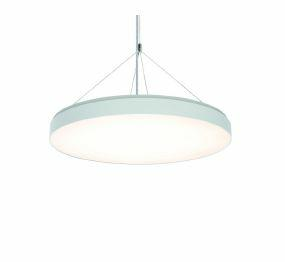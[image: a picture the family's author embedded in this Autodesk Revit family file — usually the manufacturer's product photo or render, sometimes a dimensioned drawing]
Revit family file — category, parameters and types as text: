
# Revit family: spectral_stora_stora-rp-led_4300_840_mps_c88b
name_source: partatom
category: Lighting Fixtures
revit_build: Autodesk Revit 2016 (Build: 20150220_1215(x64)
units: mm (PartAtom-declared; Revit-internal decimal feet)

## family parameters
Cut with Voids When Loaded = No
Host = Face
Light Source = No
Part Type = Normal
Room Calculation Point = No
Round Connector Dimension = Use Diameter
Shared = No

## types (1)
- SPECTRAL STORA (1 x )
    Apparent Load = 0 VA
    CIE Flux Codes = 72 94 98 100 100
    Control Gear = Electronic transformer
    Default Elevation = 1800 mm
    Description = SPC0620032
STORA pendant LED luminaire

Design:
Round luminaire element with a microprism panel mounted in a profile frame made of power-coated aluminium. The frame is fastened on the owdercoated
steel body using a bayonet catch with spring clip. The luminaire is suspended by four trapezoidal wire pendants with ceiling fixture and transparent
connecting cable with round ceiling junction box. The cable length can be adjusted at the ceiling junction box, the steel wire can be steplessly height
adjusted. The steel body houses the electrical components and electronic ballast. The LED module is formed as a round LED flat board and can be removed for mounting or exchange using a keyhole screw connection. Plug-in electrical connection of the LED flat board. The luminaire is configured with heatresistant wiring. Variant suitable for office workplaces with microprism panel MPS. The LED spots are visible as circles on the microprism panel. Light colour 4000 K (840), dimmable. Protection rating IP20, safety class I.

Colour:
Frame – similar to RAL 9016 white silk matt
    Height = 76 mm
    Lamp = 1 x
    Lamp count = 1
    Length = 420 mm
    Luminous efficacy = 0 lm/W
    Manufacturer = Ridi
    ModVariant = No
    Model = STORA-RP-LED 4300/840 MPS
    Number of Poles = 1
    OnlyDefault = Yes
    Power Factor = 1
    Product Name = SPECTRAL STORA
    Product group = Ceiling / wall-mounted luminaires
    ProductGroupID = 30
    Protection Class = Protection class
    Protection Degree = Degree of protection
    RlxData = <blob elided: 9821 chars, md5=1282cff8>
    Socket = socket
    Standby Power = 0 W
    System Light Flux = 0 lm
    System Power = 0 W
    Type Image = stora-rp.jpg
    URL = http://reluxnet.relux.com
    VarID = 1
    Voltage = 0 V
    Weight = 0.00 kg
    Width = 0 mm  [stored 0 ft]

note: [stored X ft] marks values corroborated as IEEE doubles in the binary element streams (Revit-internal decimal feet)

## geometry (parser evidence)
native form markers: Sweep x9
no freeform markers — native parametric forms only
